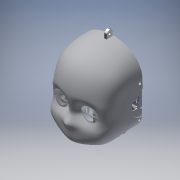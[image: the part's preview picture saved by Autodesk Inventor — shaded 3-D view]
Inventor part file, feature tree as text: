
AUTODESK INVENTOR PART (.ipt)
format: ipt  version: 2019 (Build 230136000, 136)  size: 11,228,160 bytes
history: native  units: in
note: dims shown in document units (in); Inventor stores cm internally (conversion verified against a paired STEP export)
features: extrude x67, sketch x41, other x30, plane x21, projected_geometry x15, mirror x14, pattern_linear x7, surface_op x6, fillet x5, hole x4, chamfer x3, thicken_offset x2, direct_edit x2, imported_body x2, move_body x2, split x1
ambient origin geometry x8: Origin, YZ Plane, XZ Plane, XY Plane, X Axis, Y Axis, Z Axis, Center Point
bodies: Solid2 (feature_tree)
feature tree (222):
  other  "rc_ist_009_p_077_09"
  other  "rc_ist_009_p_077_091"
  other  "Work Point1"
  other  "Work Point2"
  other  "Work Point3"
  other  "Work Point4"
  other  "Work Point5"
  other  "A_5"
  other  "A_6"
  other  "A_7"
  other  "A_8"
  other  "SIDE"
  other  "TOP"
  plane  "Work Plane4"
  plane  "Work Plane11"
  plane  "Work Plane7"
  plane  "Work Plane9"
  extrude  "Extrusion10"  Depth=0.9252in
  sketch  "Sketch11"  dims[d40=0.315in d41=0.315in]
  extrude  "Extrusion11"  Depth=0.315in
  plane  "Work Plane10"
  extrude  "Extrusion12"  Depth=1.063in TaperAngle=0.0deg
  mirror  "Mirror3"
  extrude  "Extrusion13"  Depth=1.8504in
  sketch  "Sketch15"  dims[d50=0.3543in d52=0.1969in d53=0.0in]
  extrude  "Extrusion14"  Depth=0.3543in
  extrude  "Extrusion15"  Depth=0.1969in TaperAngle=0.0deg
  extrude  "Extrusion16"  Depth=0.2362in TaperAngle=0.0deg
  extrude  "Extrusion17"  TaperAngle=180.0deg  [1 undecoded]
  extrude  "Extrusion18"  TaperAngle=90.0deg  [1 undecoded]
  extrude  "Extrusion19"  TaperAngle=90.0deg  [1 undecoded]
  hole  "Hole1"  [1 undecoded]
  hole  "Hole2"  [1 undecoded]
  extrude  "Extrusion22"  TaperAngle=60.0deg  [1 undecoded]
  extrude  "Extrusion23"  Depth=0.315in
  extrude  "Extrusion24"  Depth=0.3937in TaperAngle=0.0deg
  extrude  "Extrusion25"  TaperAngle=150.0deg  [1 undecoded]
  extrude  "Extrusion26"  TaperAngle=120.0deg  [1 undecoded]
  sketch  "Sketch34"  dims[d100=0.3937in d101=0.0in d108=0.7874in]
  sketch  "3D Sketch2"
  surface_op  "Extend2"
  thicken_offset  "Thicken5"
  plane  "Work Plane12"
  extrude  "Extrusion27"  TaperAngle=150.0deg  [1 undecoded]
  plane  "Work Plane13"
  surface_op  "Extend3"
  thicken_offset  "Thicken6"
  mirror  "Mirror4"
  plane  "Work Plane14"
  plane  "Work Plane15"
  extrude  "Extrusion29"  TaperAngle=120.0deg  [1 undecoded]
  mirror  "Mirror5"
  plane  "Work Plane16"
  extrude  "Extrusion30"  Depth=0.7874in
  mirror  "Mirror6"
  extrude  "Extrusion31"  Depth=0.4331in
  plane  "Work Plane17"
  extrude  "Extrusion32"  Depth=0.3937in
  mirror  "Mirror8"
  extrude  "Extrusion33"  Depth=0.3937in
  extrude  "Extrusion34"  Depth=0.7087in
  mirror  "Mirror9"
  split  "Split5"
  plane  "Work Plane19"
  plane  "Work Plane20"
  sketch  "Sketch51"  dims[d153=0.1969in d154=0.0in d158=0.1181in d160=0.3937in]
  plane  "Work Plane23"
  sketch  "Sketch49"  dims[d137=0.1575in d138=0.0in d139=0.3937in d140=0.0in]
  extrude  "Extrusion35"  Depth=0.5906in
  extrude  "Extrusion36"  Depth=0.3937in TaperAngle=0.0deg
  hole  "Hole4"  [1 undecoded]
  extrude  "Extrusion38"  TaperAngle=0.0deg  [1 undecoded]
  extrude  "Extrusion39"  Depth=1.0625in
  fillet  "Fillet4"  Radius=0.1969in
  extrude  "Extrusion40"  Depth=0.1575in
  mirror  "Mirror12"
  extrude  "Extrusion37"  Depth=0.3937in
  mirror  "Mirror11"
  plane  "Work Plane25"
  sketch  "Sketch53"  dims[d165=0.8465in d166=1.0625in d169=0.1969in]
  extrude  "Extrusion41"  Depth=0.315in
  extrude  "Extrusion42"  Depth=0.0787in
  hole  "Hole5"  [1 undecoded]
  extrude  "Extrusion43"  Depth=0.3937in
  extrude  "Extrusion44"  Depth=0.0787in
  plane  "Work Plane26"
  other  "Camera Sketch"
  extrude  "Extrusion47"  Depth=0.0984in
  extrude  "Extrusion45"  Depth=0.1181in
  extrude  "Extrusion46"  Depth=0.3937in TaperAngle=0.0deg
  extrude  "Extrusion48"  Depth=0.2362in
  extrude  "Extrusion49"  Depth=0.1181in TaperAngle=0.0deg
  extrude  "Extrusion53"  Depth=0.0984in
  extrude  "Extrusion54"  Depth=0.1969in
  extrude  "Extrusion55"  Depth=0.1378in
  sketch  "Sketch55"  dims[d170=0.0in d171=0.1575in d172=0.1575in]
  extrude  "Extrusion50"  Depth=0.0787in TaperAngle=0.0deg
  extrude  "Extrusion51"  Depth=0.2362in
  extrude  "Extrusion52"  Depth=0.1181in TaperAngle=0.0deg
  chamfer  "Chamfer1"  Distance=1.1024in
  extrude  "Extrusion56"  Depth=0.1374in
  extrude  "Extrusion57"  Depth=3.937in
  extrude  "Extrusion58"  Depth=3.7402in
  extrude  "Extrusion59"  Depth=0.1575in TaperAngle=0.0deg
  pattern_linear  "Rectangular Pattern1"  Spacing1=0.0787in  [1 undecoded]
  extrude  "Extrusion60"  Depth=0.0787in TaperAngle=0.0deg
  extrude  "Extrusion61"  Depth=0.1575in TaperAngle=0.0deg
  chamfer  "Chamfer2"  Distance=0.0787in
  mirror  "Mirror13"
  mirror  "Mirror14"
  mirror  "Mirror18"
  pattern_linear  "Rectangular Pattern2"  Spacing1=0.0787in  [1 undecoded]
  direct_edit  "Direct Edit1"
  direct_edit  "Direct Edit2"
  sketch  "Sketch59"  dims[d195=0.3937in d196=0.0in d197=1.7913in]
  extrude  "Extrusion62"  Depth=0.0787in TaperAngle=0.0deg
  extrude  "Extrusion63"  Depth=0.0687in
  extrude  "Extrusion64"  Depth=1.2008in
  extrude  "Extrusion65"  Depth=0.1181in TaperAngle=0.0deg
  pattern_linear  "Rectangular Pattern3"  Spacing1=0.0591in  [1 undecoded]
  chamfer  "Chamfer3"  Distance=0.0787in
  fillet  "Fillet5"  Radius=0.0787in
  extrude  "Extrusion66"  Depth=3.0118in
  pattern_linear  "Rectangular Pattern4"  Spacing1=0.0787in  [1 undecoded]
  plane  "Work Plane27"
  extrude  "Extrusion67"  Depth=0.0787in TaperAngle=0.0deg
  extrude  "Extrusion69"  Depth=1.7717in
  sketch  "Sketch63"  dims[d200=0.315in d201=0.3937in]
  extrude  "Extrusion70"  Depth=0.315in TaperAngle=0.0deg
  extrude  "Extrusion71"  Depth=0.4134in TaperAngle=0.0deg
  pattern_linear  "Rectangular Pattern5"  Spacing1=0.0591in  [1 undecoded]
  pattern_linear  "Rectangular Pattern6"  Spacing1=0.0591in  [1 undecoded]
  mirror  "Mirror15"
  fillet  "Fillet6"  Radius=0.0394in
  mirror  "Mirror16"
  extrude  "Extrusion72"  Depth=0.0394in
  extrude  "Extrusion73"  Depth=0.1181in TaperAngle=0.0deg
  extrude  "Extrusion74"  Depth=0.1181in TaperAngle=0.0deg
  fillet  "Fillet7"  Radius=0.0787in
  sketch  "Sketch64"  dims[d202=0.0in d203=0.0787in]
  extrude  "Extrusion75"  Depth=0.0787in
  extrude  "Extrusion76"  Depth=0.0787in
  plane  "Work Plane28"
  sketch  "Sketch65"  dims[d204=0.3937in d205=0.0in d213=0.0984in]
  extrude  "Extrusion77"  Depth=0.0787in
  extrude  "Extrusion78"  Depth=0.7874in TaperAngle=0.0deg
  extrude  "Extrusion79"  Depth=0.0787in TaperAngle=45.0deg
  fillet  "Fillet8"  Radius=0.2362in
  pattern_linear  "Rectangular Pattern7"  Spacing1=0.0787in  [1 undecoded]
  mirror  "Mirror17"
  sketch  "3D Sketch1"
  other  "FRONT"
  imported_body  "Base1"
  imported_body  "Base2"
  plane  "Work Plane8"
  sketch  "Sketch10"  dims[d3=3.563in d35=0.9252in]
  sketch  "Sketch12"  dims[d42=0.315in d43=1.063in d44=0.0in]
  sketch  "Sketch13"  dims[d45=0.9252in d46=1.8504in]
  sketch  "Sketch14"  dims[d47=2.3622in d48=0.0in d49=0.3543in]
  sketch  "Sketch16"  dims[d55=0.1969in d56=0.0in d59=0.2362in d60=0.0in]
  sketch  "Sketch17"  dims[d61=0.3937in d62=180.0deg]
  projected_geometry  "Projected Loop7"
  projected_geometry  "Projected Loop8"
  projected_geometry  "Projected Loop9"
  sketch  "Sketch18"  dims[d63=1.1811in d64=90.0deg]
  projected_geometry  "Projected Loop10"
  sketch  "Sketch19"  dims[d65=0.3937in d66=90.0deg]
  projected_geometry  "Projected Loop11"
  sketch  "Sketch21"  dims[d67=3.937in d68=0.0in d73=0.3937in]
  sketch  "Sketch22"  dims[d75=3.937in d76=0.0in d77=3.937in d78=0.0in]
  sketch  "Sketch26"  dims[d85=0.315in d86=60.0deg]
  sketch  "Sketch27"  dims[d87=30.0deg d88=0.315in]
  sketch  "Sketch29"  dims[d89=60.0deg d90=0.3937in d91=0.0in]
  sketch  "Sketch30"  dims[d92=0.1969in d93=150.0deg]
  sketch  "Sketch31"  dims[d94=0.1969in d95=120.0deg]
  sketch  "Sketch32"  dims[d96=0.1969in d97=150.0deg]
  sketch  "Sketch33"  dims[d98=0.1969in d99=120.0deg]
  other  "Srf6"
  other  "Eye Sockets"
  sketch  "Sketch35"  dims[d109=0.2953in]
  other  "Srf7"
  other  "Srf11"
  other  "Srf10"
  sketch  "Sketch38"  dims[d110=0.2953in d111=0.2362in d112=0.1575in d113=0.0787in d114=90.0deg d115=0.315in d116=0.8108in d117=0.4331in]
  sketch  "Sketch39"  dims[d118=0.4724in d119=0.2362in d120=0.1575in d121=0.0787in d122=90.0deg d123=0.1969in d124=0.0in d127=0.3937in]
  sketch  "Sketch41"  dims[d128=0.1969in d129=0.0in d130=0.3937in]
  sketch  "Sketch42"  dims[d131=0.1969in d132=0.0in d133=0.7087in]
  sketch  "Sketch43"  dims[d134=0.1575in d135=0.0in d136=0.5906in]
  projected_geometry  "Projected Loop12"
  plane  "Work Plane22"
  other  "Eyebrows subassembly"
  other  "Supports"
  sketch  "Sketch52"  dims[d161=-0.815in d162=0.0in d163=0.0in]
  projected_geometry  "Projected Loop13"
  plane  "Work Plane24"
  other  "Mouth subassembly"
  other  "Camera subassembly"
  other  "Camera covers"
  other  "Camera supports"
  sketch  "Sketch56"  dims[d173=0.1575in d185=0.3937in]
  projected_geometry  "Projected Loop14"
  sketch  "Sketch57"  dims[d190=0.0in d191=-1.6063in d192=0.315in]
  projected_geometry  "Projected Loop15"
  sketch  "Sketch58"  dims[d193=0.3937in d194=0.0787in]
  other  "Srf13"
  projected_geometry  "Projected Loop16"
  projected_geometry  "Projected Loop17"
  projected_geometry  "Projected Loop19"
  projected_geometry  "Projected Loop20"
  other  "Cable clamps"
  projected_geometry  "Projected Loop21"
  projected_geometry  "Projected Loop22"
  sketch  "Sketch66"  dims[d214=0.1969in d215=0.1181in d216=0.3937in d217=0.0in d218=0.2362in d219=0.1181in d220=0.0in d221=0.0984in d222=0.1969in d223=0.1378in d224=0.0787in d225=0.0in d226=0.2362in d227=0.1181in d228=0.0in d229=1.1024in d230=0.1374in d232=1.5748in d233=0.0in d234=1.2992in d235=1.2992in d236=1.1in d237=1.44in d238=1.4in d239=1.1in d240=0.2362in d241=0.1575in d242=0.2362in d243=0.2362in d244=0.2362in d245=0.2362in d246=0.0984in d247=0.0787in d248=0.2362in d249=0.2559in d250=3.937in d251=-0.0859in d252=3.7402in d253=0.1575in d254=0.0in d255=0.0787in d256=0.0in d257=0.0591in d258=0.2362in d259=0.0984in d260=0.0787in d261=90.0deg d262=0.315in d263=0.8108in d264=0.0787in d265=0.0in d266=0.1575in d267=0.0in d268=0.0787in d269=0.0in d270=0.0787in d277=0.0787in d278=0.0in d279=0.0687in d280=3.6614in d281=2.874in d282=1.2795in d283=0.1181in d284=0.0787in d285=1.2008in d286=1.2795in d287=1.2795in d288=0.0787in d289=1.7717in d290=0.0787in d291=1.7717in d292=0.2362in d293=0.2362in d294=0.0984in d295=0.0984in d296=1.2008in d297=0.1181in d298=0.0in d299=0.0591in d300=0.0in d301=0.0591in d302=0.2362in d303=0.0984in d304=0.0787in d305=90.0deg d306=0.315in d307=0.8108in d308=0.0787in d309=0.0in d310=0.0787in d311=0.0in d312=3.0118in d313=1.2008in d314=1.2008in d315=0.7874in d316=0.7874in d317=0.7874in d318=0.1181in d319=0.1181in d320=0.0in d321=0.0787in d322=0.0in d323=0.0787in d324=0.0in d325=1.7717in d326=0.315in d327=0.0in d328=0.4134in d329=0.0in d330=0.0591in d331=0.0591in d332=0.0394in d333=0.0394in d338=0.1181in d339=0.0in d340=0.1181in d341=0.0in d342=0.0787in d343=0.0787in d344=0.0787in d345=0.0787in d346=0.7874in d347=0.0in d348=0.0787in d349=0.0787in d350=45.0deg d351=0.2362in d352=0.0787in d353=0.0984in d354=0.2362in d355=0.2165in d356=0.0787in d357=0.0984in d358=0.2165in d359=0.2362in d360=0.3937in d361=0.0in d362=0.0787in d363=0.0in d364=0.0394in d365=0.0in d366=0.1181in d367=0.1181in d368=0.0197in d369=0.1181in d370=0.1181in d371=0.1181in d372=0.1181in d373=0.0197in d374=0.1181in d375=0.1181in d376=0.3937in d377=0.3937in d378=0.0394in d379=0.0in d380=0.1181in d381=0.0in d382=0.0394in d383=0.0in d384=0.1181in d385=0.315in d386=0.1181in d387=0.1969in d388=0.1181in d389=0.0in d390=1.1811in d392=0.1969in d395=0.1181in d396=0.0in d397=0.1181in d398=0.0in d399=0.7874in d401=2.7544in d402=0.0in d403=0.0in d404=-0.748in d405=0.0in d406=0.0in d407=-0.6299in d408=0.0197in d409=0.0787in d410=45.0deg d413=2.4016in d415=5.4602in d416=1.6535in d417=1.6535in d418=1.6929in d419=0.7874in d420=0.0in d421=2.0079in d422=1.0039in d423=0.0394in d424=0.0591in d425=0.0591in d426=1.2598in d427=1.7913in d428=0.7874in d429=0.0689in d430=0.0689in d431=0.1575in d432=0.0in d433=0.0787in d434=0.0in d435=0.1378in d436=0.0787in d437=0.0in d438=0.0in d439=0.0591in d440=0.0591in d441=1.5748in d442=0.1969in d443=0.1378in d444=0.0in d445=1.1811in d447=0.315in d448=0.0394in d449=0.0787in d450=45.0deg d451=0.2362in d457=0.3937in d458=0.0in d459=0.7874in d461=0.9843in d462=0.0787in d463=-1.3386in d465=0.0984in d466=0.0984in d467=0.5512in d468=0.0984in d469=0.0984in d470=0.0787in d471=0.0787in d472=0.3937in d473=0.0in d476=0.2362in d479=0.1969in d481=0.1772in d482=0.1181in d483=0.0in d484=0.0591in d485=0.1969in d486=0.0591in d487=0.2362in d488=0.2362in d489=0.1181in d490=0.0in d491=0.0984in d492=0.0984in d493=0.0394in d494=0.0in d495=0.7874in d497=0.5512in d498=0.7874in d500=0.5512in d501=0.1969in d504=0.0984in d505=0.0984in d506=0.5512in d507=0.0984in d508=0.0984in d509=0.0787in d510=0.0787in d511=0.2362in d512=0.1969in d513=0.0591in d514=0.1969in d515=0.0591in d516=0.1969in d517=0.0591in d518=0.1181in d519=0.0in d520=0.1181in d521=0.0in d522=0.3937in d523=0.0in d524=0.0787in d525=0.7874in d526=0.0394in d527=0.0984in d528=0.0984in d529=0.2362in d530=0.2362in d531=0.1181in d532=0.0in d533=0.0394in d534=0.0in d535=-2.7953in d537=0.3937in d538=0.0in d539=0.6693in d540=0.5118in d541=0.0787in d542=0.5906in d543=0.5906in d544=0.3937in d545=0.0in d546=0.0591in d547=0.0787in d548=0.0787in d549=0.0984in d550=0.0787in d551=0.0591in d552=0.1181in d553=0.0in d554=0.0197in d555=1.1811in d557=0.1969in d559=0.0197in d618=0.1575in d619=0.2362in d621=0.7874in d622=0.3937in d623=0.6299in d624=0.1969in]
  surface_op  "Boundary Patch2"
  surface_op  "Boundary Patch3"
  extrude  "ExtrusionSrf1"  Depth=0.0984in
  surface_op  "Boundary Patch6"
  surface_op  "Boundary Patch7"
  move_body  "Move1"
  move_body  "Move2"
  other  "Support structure"
  other  "Main shell"
note: 20 required parameter values undecoded (feature->parameter linkage not recoverable at this tier; creation-order binding heuristic only, values carry confidence <= 0.55)
